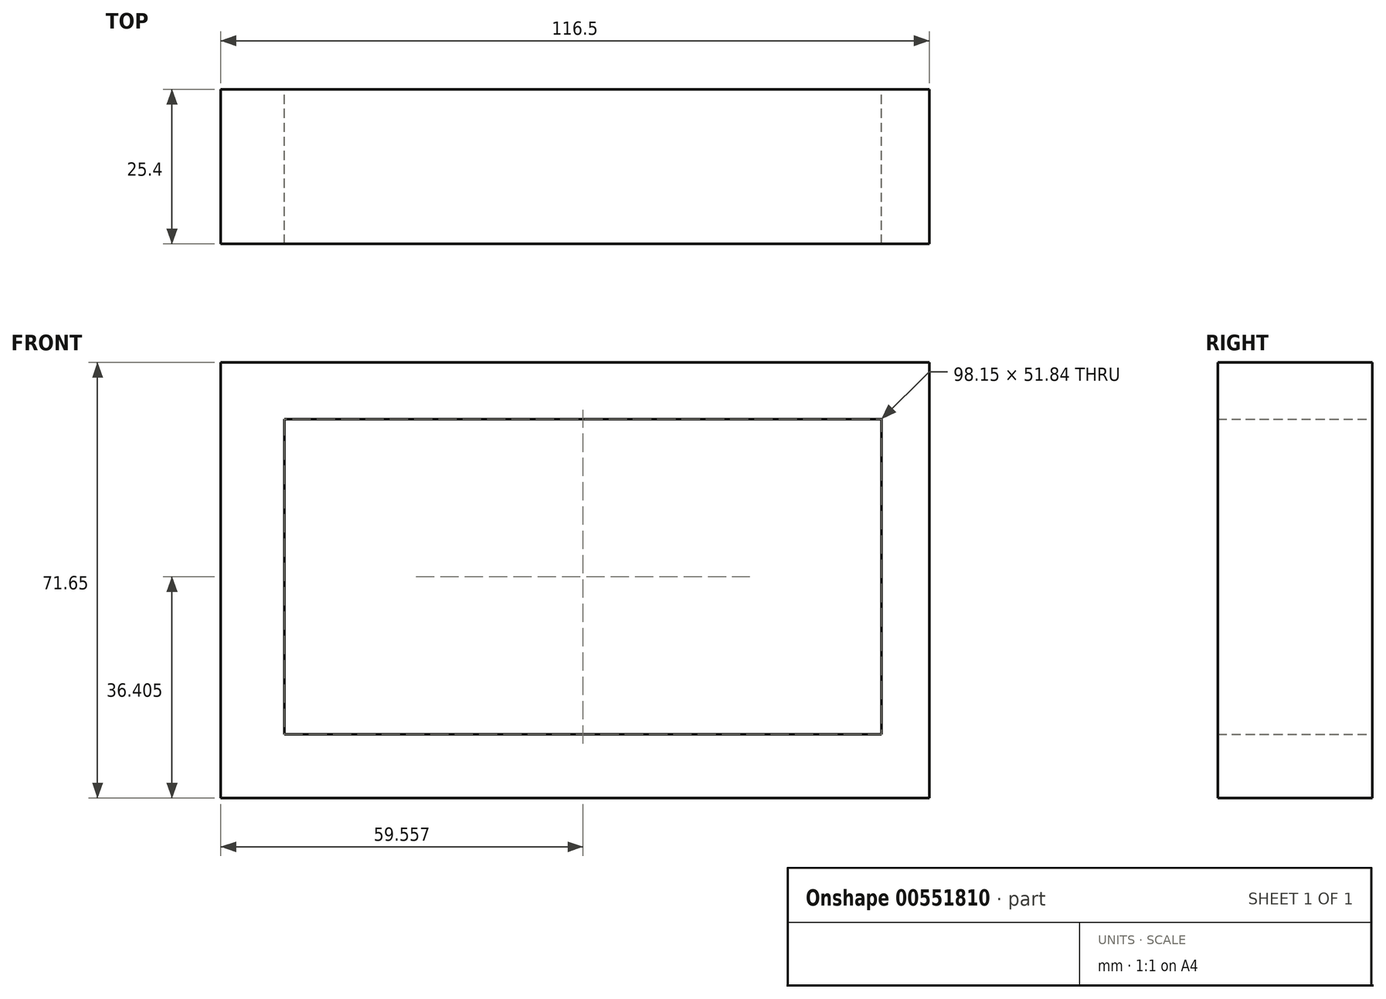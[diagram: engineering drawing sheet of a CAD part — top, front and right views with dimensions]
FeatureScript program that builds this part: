
annotation { "Feature Type Name" : "Feature", "Feature Type Description" : "" }
export const myFeature = defineFeature(function(context is Context, id is Id, definition is map)
    precondition{}
    {
        {
            var Q0;
            Q0=qCreatedBy(makeId("Front.planeOp"),FACE);
            var sketch = newSketch(context, id + "F0", { "sketchPlane" : qUnion([Q0])});
            skLineSegment(sketch, "E0.bottom", {"start": v(-53.52, 44.5) * mm, "end": v(62.98, 44.5) * mm});
            skLineSegment(sketch, "E0.top", {"start": v(-53.52, -27.14) * mm, "end": v(62.98, -27.14) * mm});
            skLineSegment(sketch, "E0.left", {"start": v(-53.52, 44.5) * mm, "end": v(-53.52, -27.14) * mm});
            skLineSegment(sketch, "E0.right", {"start": v(62.98, 44.5) * mm, "end": v(62.98, -27.14) * mm});
            skLineSegment(sketch, "E1.bottom", {"start": v(-43.04, 35.19) * mm, "end": v(55.11, 35.19) * mm});
            skLineSegment(sketch, "E1.top", {"start": v(-43.04, -16.66) * mm, "end": v(55.11, -16.66) * mm});
            skLineSegment(sketch, "E1.left", {"start": v(-43.04, 35.19) * mm, "end": v(-43.04, -16.66) * mm});
            skLineSegment(sketch, "E1.right", {"start": v(55.11, 35.19) * mm, "end": v(55.11, -16.66) * mm});
            skSolve(sketch);
        }
        {
            var Q0;
            Q0 = qSketchRegion(id + "F0", true);
            extrude(context, id + "F1", {"entities" : qUnion([Q0]), "depth" : 25.4 * mm, "offsetDistance" : 25.4 * mm});
        }
    });
